# Revit family: ASH_ArmitageShanks_WCPans_Contour21_S3046
name_source: partatom
category: Plumbing Fixtures
revit_build: Autodesk Revit MEP 2012 (Build: 20110309_2315(x64)
units: mm (PartAtom-declared; Revit-internal decimal feet)

## types (1)
- S304601 - Contour 21 Back To Wall/Close Coupled WC Pan 305mm high
    Accessories = www.idealspec.co.uk
    AreaUnits = millimeters
    Assembly Code = C1030200
    AssetType = Fixed
    BIMObjectName = ASH_ArmitageShanks_WCPans_Contour21-305 mmHigh_S3046
    Brand = Armitage Shanks
    CWFU = 0
    Color = White
    ConnectionType = Plumbing
    Default Elevation = 0 mm  [stored 0 ft]
    Description = Contour 21 back-to-wall/close coupled wc pan 305 mm high
    DurationUnit = year
    ECA = Yes
    ExpectedLife = 30
    Features = back-to-wall/close coupled wc pan 305 mm high
    Finish = White
    HWFU = 0
    Help = www.idealspec.co.uk/contact-us.html
    IfcExportAs = IfcSanitaryTerminalType
    IfcExportType = TOILETPAN
    InstallationInstructions = www.idealspec.co.uk/resources.html
    LinearUnits = millimeters
    ManufacturerURL = www.idealspec.co.uk
    Material = Vitreous china
    Model = S304601
    ModelNumber = S304601
    ModelReference = Contour 21 back-to-wall/close coupled wc pan 305 mm high
    NBSDescription = WC pans
    NBSReference = 45-36-70/384
    Name = WCPans_Contour21-305 mmHigh-S3046_ArmitageShanks
    NettWeight = 15Kg
    NominalDepth = 490 mm  [stored 1.60761 ft]
    NominalHeight = 305 mm
    NominalLength = 490 mm  [stored 1.60761 ft]
    NominalWidth = 315 mm  [stored 1.03346 ft]
    PanColor = White
    PanMaterial = Vitreous china
    PanMounting = BackToWall
    ProductInformation = www.idealspec.co.uk/assets/datasheet/S304601
    Shape = Sculptured
    Size = 490 x 315 x 305 mm
    Space = Internal
    SpareParts = www.fastpart-spares.co.uk
    SpilloverLevel = 0 mm  [stored 0 ft]
    ToiletPanType = WashDown
    ToiletType = Other
    URL = www.idealspec.co.uk
    Uniclass2 = Pr_40_20_93_94
    Version = 2
    VolumeUnits = Litres
    WFU = 0
    WRAS = No
    WarrantyDescription = Manufacturers Warranty
    WarrantyDurationParts = 99
    WarrantyDurationUnit = year
    WaterEfficientProduct = Yes

note: [stored X ft] marks values corroborated as IEEE doubles in the binary element streams (Revit-internal decimal feet)

## geometry (parser evidence)
native form markers: Blend x2, Sweep x4
no freeform markers — native parametric forms only
